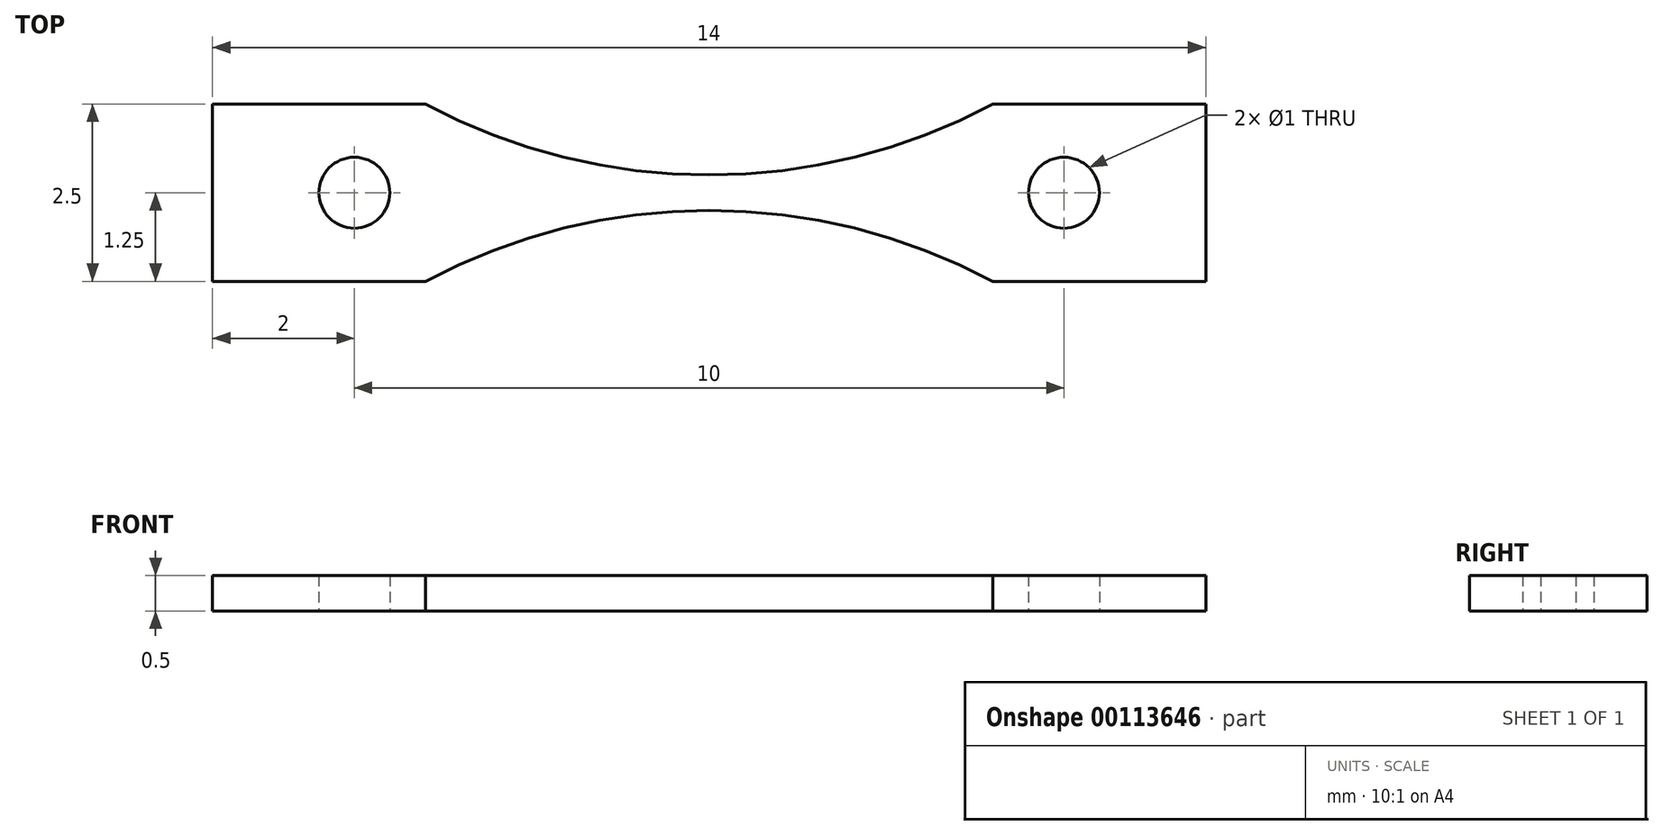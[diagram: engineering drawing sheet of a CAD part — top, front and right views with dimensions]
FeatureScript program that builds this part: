
annotation { "Feature Type Name" : "Feature", "Feature Type Description" : "" }
export const myFeature = defineFeature(function(context is Context, id is Id, definition is map)
    precondition{}
    {
        {
            var Q0;
            Q0=qCreatedBy(makeId("Top.planeOp"),FACE);
            var sketch = newSketch(context, id + "F0", { "sketchPlane" : qUnion([Q0])});
            skLineSegment(sketch, "E0", {"start": v(-7, 0) * mm, "end": v(-7, 1.25) * mm});
            skCircle(sketch, "E1", {"center": v(-5, 0) * mm, "radius": 0.5 * mm});
            skPoint(sketch, "E2", {"position": v(0, 8.75) * mm});
            skPoint(sketch, "E3", {"position": v(0, 0.25) * mm});
            skLineSegment(sketch, "E4", {"start": v(-7, 1.25) * mm, "end": v(0, 1.25) * mm, "construction": true});
            skArc(sketch, "E5", {"start": v(0, 0.25) * mm, "mid": v(-2.06, 0.5) * mm, "end": v(-4, 1.25) * mm});
            skLineSegment(sketch, "E6", {"start": v(-4, 1.25) * mm, "end": v(-7, 1.25) * mm});
            skLineSegment(sketch, "E7.MirrorCS", {"start": v(-7, 0) * mm, "end": v(-7, -1.25) * mm});
            skLineSegment(sketch, "E8.MirrorCS", {"start": v(-7, -1.25) * mm, "end": v(0, -1.25) * mm, "construction": true});
            skLineSegment(sketch, "E9.MirrorCS", {"start": v(-4, -1.25) * mm, "end": v(-7, -1.25) * mm});
            skArc(sketch, "E10.MirrorCS", {"start": v(0, -0.25) * mm, "mid": v(-2.06, -0.5) * mm, "end": v(-4, -1.25) * mm});
            skLineSegment(sketch, "E11.MirrorCS", {"start": v(4, 1.25) * mm, "end": v(7, 1.25) * mm});
            skLineSegment(sketch, "E12.MirrorCS", {"start": v(4, -1.25) * mm, "end": v(7, -1.25) * mm});
            skLineSegment(sketch, "E13.MirrorCS", {"start": v(7, 0) * mm, "end": v(7, 1.25) * mm});
            skArc(sketch, "E14.MirrorCS", {"start": v(0, -0.25) * mm, "mid": v(2.06, -0.5) * mm, "end": v(4, -1.25) * mm});
            skCircle(sketch, "E15.MirrorC", {"center": v(5, 0) * mm, "radius": 0.5 * mm});
            skLineSegment(sketch, "E16.MirrorCS", {"start": v(7, 0) * mm, "end": v(7, -1.25) * mm});
            skLineSegment(sketch, "E17.MirrorCS", {"start": v(7, -1.25) * mm, "end": v(0, -1.25) * mm, "construction": true});
            skLineSegment(sketch, "E18.MirrorCS", {"start": v(7, 1.25) * mm, "end": v(0, 1.25) * mm, "construction": true});
            skArc(sketch, "E19.MirrorCS", {"start": v(0, 0.25) * mm, "mid": v(2.06, 0.5) * mm, "end": v(4, 1.25) * mm});
            skSolve(sketch);
        }
        {
            var Q0;
            Q0=makeQuery(id+"F0.imprint","IMPRINT",FACE,{"disambiguationData":[TD([[makeQuery(id+"F0.imprint","IMPRINT",EDGE,{"derivedFrom":sQuery(id+"F0.wireOp",EDGE,"E0")}),-1.0]])]});
            extrude(context, id + "F1", {"entities" : qUnion([Q0]), "depth" : 0.5 * mm, "offsetDistance" : 25 * mm, "symmetric" : true});
        }
    });
